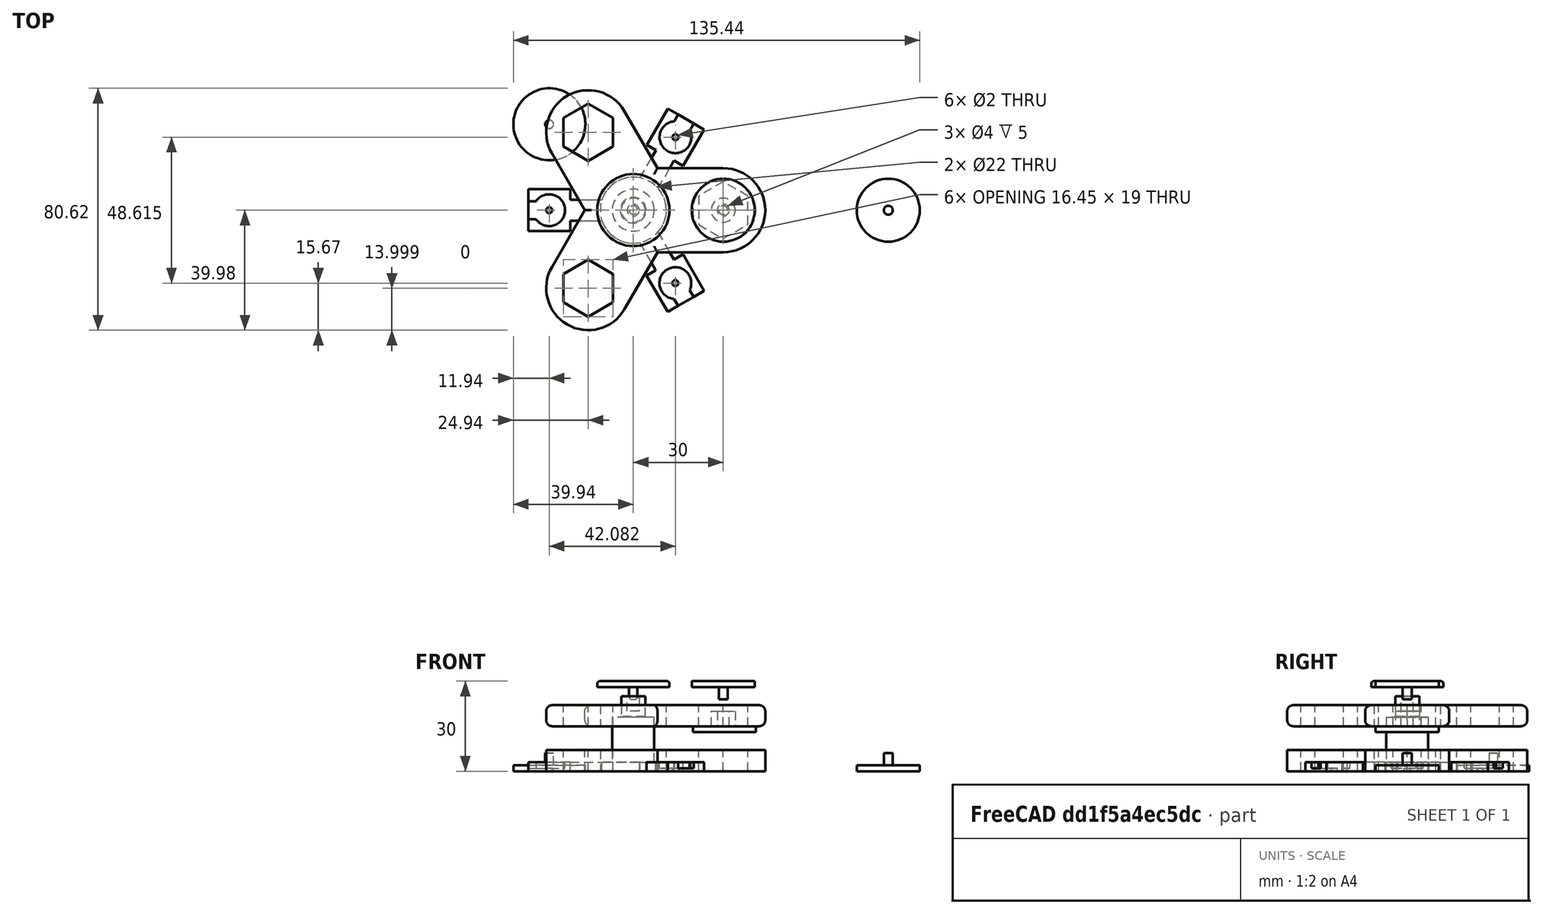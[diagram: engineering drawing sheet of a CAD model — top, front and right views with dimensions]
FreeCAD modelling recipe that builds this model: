
FCSTD DOCUMENT  (FreeCAD 0.17R9747 (Git))
Label: Spinner-ZZ809-M10
License: All rights reserved
LicenseURL: http://en.wikipedia.org/wiki/All_rights_reserved
objects: Sketcher::SketchObject×16, PartDesign::Pad×10, PartDesign::Pocket×6, PartDesign::Body×5, Part::FeaturePython×5, Part::Fillet×4, Mesh::Feature×4, App::DocumentObjectGroup×2, Part::Chamfer×1
note: 63 computed .brp shape members not serialized (recipe doc carries the construction recipe); baked Part::Feature solids carry a one-line shape summary decoded from their .brp

FEATURE [Sketcher::SketchObject] Sketch001  label="Sketch-base"
  MapMode = 5
  Support = -> [XY_Plane001]
  sketch-geometry (28):
    g0: ArcOfCircle CenterX=0.0583268 CenterY=0 CenterZ=0 NormalX=0 NormalY=0 NormalZ=1 Radius=11 StartAngle=3.4654 EndAngle=4.90733
    g1: LineSegment [constr] StartX=0 StartY=0 StartZ=0 EndX=-28 EndY=0 EndZ=0
    g2: LineSegment [constr] StartX=0 StartY=0 StartZ=0 EndX=14 EndY=24.2487 EndZ=0
    g3: LineSegment [constr] StartX=0 StartY=0 StartZ=0 EndX=14 EndY=-24.2487 EndZ=0
    g4: LineSegment StartX=-35 StartY=7 StartZ=0 EndX=-21 EndY=7 EndZ=0
    g5: LineSegment StartX=-21 StartY=7 StartZ=0 EndX=-21 EndY=3.5 EndZ=0
    g6: LineSegment StartX=-21 StartY=-7 StartZ=0 EndX=-35 EndY=-7 EndZ=0
    g7: LineSegment StartX=-35 StartY=-7 StartZ=0 EndX=-35 EndY=7 EndZ=0
    g8: LineSegment StartX=-21 StartY=3.5 StartZ=0 EndX=-10.37 EndY=3.5 EndZ=0
    g9: LineSegment StartX=-21 StartY=-3.5 StartZ=0 EndX=-10.37 EndY=-3.5 EndZ=0
    g10: LineSegment StartX=-21 StartY=-3.5 StartZ=0 EndX=-21 EndY=-7 EndZ=0
    g11: LineSegment StartX=4.51981 StartY=21.7433 StartZ=0 EndX=7.5509 EndY=19.9933 EndZ=0
    g12: LineSegment StartX=2.23326 StartY=10.7828 StartZ=0 EndX=7.5509 EndY=19.9933 EndZ=0
    g13: LineSegment StartX=8.29808 StartY=7.28742 StartZ=0 EndX=13.6131 EndY=16.4933 EndZ=0
    g14: LineSegment StartX=13.6131 StartY=16.4933 StartZ=0 EndX=16.6442 EndY=14.7433 EndZ=0
    g15: ArcOfCircle CenterX=0.0583268 CenterY=0 CenterZ=0 NormalX=0 NormalY=0 NormalZ=1 Radius=11 StartAngle=1.37176 EndAngle=2.81778
    g16: LineSegment StartX=4.51981 StartY=21.7433 StartZ=0 EndX=11.5198 EndY=33.8676 EndZ=0
    g17: LineSegment StartX=11.5198 StartY=33.8676 StartZ=0 EndX=23.6442 EndY=26.8676 EndZ=0
    g18: LineSegment StartX=16.6442 StartY=14.7433 StartZ=0 EndX=23.6442 EndY=26.8676 EndZ=0
    g19: LineSegment [constr] StartX=14 StartY=24.2487 StartZ=0 EndX=17.0311 EndY=22.4987 EndZ=0
    g20: LineSegment StartX=4.47302 StartY=-21.7475 StartZ=0 EndX=7.50411 EndY=-19.9975 EndZ=0
    g21: LineSegment StartX=8.26824 StartY=-7.32102 StartZ=0 EndX=13.5663 EndY=-16.4975 EndZ=0
    g22: LineSegment StartX=2.18911 StartY=-10.7917 StartZ=0 EndX=7.50411 EndY=-19.9975 EndZ=0
    g23: ArcOfCircle CenterX=0.0583268 CenterY=0 CenterZ=0 NormalX=0 NormalY=0 NormalZ=1 Radius=11 StartAngle=5.55496 EndAngle=7.00733
    g24: LineSegment StartX=13.5663 StartY=-16.4975 StartZ=0 EndX=16.5974 EndY=-14.7475 EndZ=0
    g25: LineSegment StartX=16.5974 StartY=-14.7475 StartZ=0 EndX=23.5974 EndY=-26.8719 EndZ=0
    g26: LineSegment StartX=23.5974 StartY=-26.8719 StartZ=0 EndX=11.473 EndY=-33.8719 EndZ=0
    g27: LineSegment StartX=11.473 StartY=-33.8719 StartZ=0 EndX=4.47302 EndY=-21.7475 EndZ=0
  constraints (83):
    c: Coincident(g1,g-1)
    c: Coincident(g2,g-1)
    c: Coincident(g3,g-1)
    c: Equal(g1,g2)
    c: Equal(g2,g3)
    c: Angle(g2,g1) = 2.0944
    c: Angle(g3,g2) = 2.0944
    c: DistanceX(g1,g1) = 28
    c: Coincident(g4,g5)
    c: Coincident(g10,g6)
    c: Coincident(g6,g7)
    c: Coincident(g7,g4)
    c: Horizontal(g4)
    c: Horizontal(g6)
    c: Vertical(g5)
    c: Vertical(g7)
    c: Symmetric(g4,g10,g1)
    c: DistanceX(g4,g4) = 14
    c: Radius(g0) = 11
    c: Horizontal(g8)
    c: Horizontal(g9)
    c: Tangent(g5,g10)
    c: Coincident(g9,g0)
    c: Coincident(g8,g15)
    c: Coincident(g8,g5)
    c: Coincident(g10,g9)
    c: DistanceY(g9,g5) = 7
    c: DistanceY(g7,g7) = 14
    c: DistanceY(g10,g10) = 3.5
    c: Equal(g8,g9)
    c: Symmetric(g0,g15,g1)
    c: DistanceX(g9,g9) = 10.63
    c: Angle(g14,g2) = 1.5708
    c: Angle(g12,g11) = 1.5708
    c: Parallel(g2,g12)
    c: Parallel(g2,g13)
    c: Coincident(g11,g12)
    c: Tangent(g11,g14)
    c: Equal(g0,g15)
    c: Coincident(g0,g15)
    c: Coincident(g12,g15)
    c: Coincident(g13,g23)
    c: Coincident(g13,g14)
    c: Distance(g12,g23) = 7
    c: Equal(g14,g11)
    c: Distance(g11) = 3.5
    c: Coincident(g16,g11)
    c: Coincident(g17,g16)
    c: Coincident(g18,g14)
    c: Coincident(g18,g17)
    c: Distance(g13) = 10.63
    c: Angle(g16,g17) = 1.5708
    c: Distance(g17) = 14
    c: Equal(g18,g17)
    c: Equal(g17,g16)
    c: Coincident(g19,g2)
    c: Angle(g2,g19) = 1.5708
    c: Distance(g19) = 3.5
    c: Distance(g13,g19) = 6.91
    c: Angle(g3,g24) = 1.5708
    c: Parallel(g21,g3)
    c: Parallel(g22,g3)
    c: Equal(g0,g23)
    c: Coincident(g0,g23)
    c: Tangent(g20,g24)
    c: Coincident(g21,g24)
    c: Coincident(g22,g20)
    c: Coincident(g22,g0)
    c: Coincident(g21,g23)
    c: Equal(g20,g24)
    c: Distance(g24) = 3.5
    c: Distance(g0,g21) = 7
    c: Symmetric(g20,g21,g3)
    c: Distance(g22) = 10.63
    c: Coincident(g24,g25)
    c: Coincident(g25,g26)
    c: Coincident(g26,g27)
    c: Coincident(g27,g20)
    c: Angle(g25,g26) = 1.5708
    c: Angle(g26,g27) = 1.5708
    c: Distance(g26) = 14
    c: Equal(g27,g25)
    c: Equal(g25,g26)
FEATURE [PartDesign::Pad] Pad  label="Base-inicial"
  Length = 3
  Length2 = 100
  Profile = -> Sketch001
  Type = 0
FEATURE [Sketcher::SketchObject] Sketch  label="Sketch-rebajes-chinchetas"
  ExternalGeometry = -> [Pad]
  MapMode = 5
  Placement = pos=(0,0,3) rot=(0,0,1;0rad)
  Support = -> [Pad]
  sketch-geometry (20):
    g0: LineSegment [constr] StartX=-35 StartY=7 StartZ=0 EndX=-21 EndY=-7 EndZ=0
    g1: LineSegment [constr] StartX=-35 StartY=-7 StartZ=0 EndX=-28 EndY=-3e-12 EndZ=0
    g2: ArcOfCircle CenterX=-28 CenterY=-3e-12 CenterZ=0 NormalX=0 NormalY=0 NormalZ=1 Radius=5.3 StartAngle=3.74328 EndAngle=8.82309
    g3: LineSegment StartX=-36.3692 StartY=3 StartZ=0 EndX=-32.3692 EndY=3 EndZ=0
    g4: LineSegment StartX=-36.3692 StartY=-3 StartZ=0 EndX=-32.3692 EndY=-3 EndZ=0
    g5: LineSegment StartX=-36.3692 StartY=3 StartZ=0 EndX=-36.3692 EndY=-3 EndZ=0
    g6: LineSegment [constr] StartX=4.47302 StartY=-21.7475 StartZ=0 EndX=23.5974 EndY=-26.8719 EndZ=0
    g7: LineSegment [constr] StartX=14.0352 StartY=-24.3097 StartZ=0 EndX=16.5974 EndY=-14.7475 EndZ=0
    g8: LineSegment [constr] StartX=0 StartY=0 StartZ=0 EndX=19 EndY=-32.909 EndZ=0
    g9: LineSegment [constr] StartX=4.51981 StartY=21.7433 StartZ=0 EndX=14.082 EndY=24.3054 EndZ=0
    g10: LineSegment [constr] StartX=11.5198 StartY=33.8676 StartZ=0 EndX=16.6442 EndY=14.7433 EndZ=0
    g11: LineSegment [constr] StartX=0 StartY=0 StartZ=0 EndX=19.0499 EndY=32.8801 EndZ=0
    g12: ArcOfCircle CenterX=14.0352 CenterY=-24.3097 CenterZ=0 NormalX=0 NormalY=0 NormalZ=1 Radius=5.3 StartAngle=5.83768 EndAngle=10.9175
    g13: ArcOfCircle CenterX=14.082 CenterY=24.3054 CenterZ=0 NormalX=0 NormalY=0 NormalZ=1 Radius=5.3 StartAngle=1.64834 EndAngle=6.72621
    g14: LineSegment StartX=16.4019 StartY=-34.409 StartZ=0 EndX=13.6217 EndY=-29.5935 EndZ=0
    g15: LineSegment StartX=21.5981 StartY=-31.409 StartZ=0 EndX=18.8179 EndY=-26.5935 EndZ=0
    g16: LineSegment StartX=16.4019 StartY=-34.409 StartZ=0 EndX=21.5981 EndY=-31.409 EndZ=0
    g17: LineSegment StartX=13.6714 StartY=29.5895 StartZ=0 EndX=16.4505 EndY=34.3861 EndZ=0
    g18: LineSegment StartX=16.4505 StartY=34.3861 StartZ=0 EndX=21.6421 EndY=31.3783 EndZ=0
    g19: LineSegment StartX=21.6421 StartY=31.3783 StartZ=0 EndX=18.8703 EndY=26.5774 EndZ=0
  constraints (58):
    c: Coincident(g0,g-4)
    c: Coincident(g1,g-4)
    c: PointOnObject(g1,g0)
    c: Coincident(g2,g1)
    c: Radius(g2) = 5.3
    c: Coincident(g0,g-5)
    c: Angle(g-4,g1) = 0.785398
    c: Horizontal(g3)
    c: Horizontal(g4)
    c: Coincident(g2,g4)
    c: Coincident(g2,g3)
    c: DistanceY(g2,g2) = 6
    c: Equal(g3,g4)
    c: Coincident(g5,g3)
    c: Vertical(g5)
    c: Coincident(g5,g4)
    c: DistanceX(g3,g3) = 4
    c: Coincident(g6,g-6)
    c: Coincident(g6,g-8)
    c: Coincident(g7,g-7)
    c: PointOnObject(g7,g6)
    c: Angle(g7,g-7) = 0.785398
    c: Coincident(g8,g-1)
    c: PointOnObject(g7,g8)
    c: Distance(g8) = 38
    c: Coincident(g9,g-9)
    c: Coincident(g10,g-10)
    c: Coincident(g10,g-11)
    c: PointOnObject(g9,g10)
    c: Angle(g9,g-9) = 0.785398
    c: Coincident(g11,g-1)
    c: PointOnObject(g9,g11)
    c: Distance(g11) = 38
    c: Coincident(g12,g7)
    c: Radius(g12) = 5.3
    c: Coincident(g13,g9)
    c: Radius(g13) = 5.3
    c: Parallel(g15,g14)
    c: PointOnObject(g12,g14)
    c: Coincident(g12,g15)
    c: Symmetric(g12,g12,g8)
    c: Distance(g14,g15) = 6
    c: PointOnObject(g8,g16)
    c: Coincident(g14,g16)
    c: Coincident(g15,g16)
    c: Coincident(g12,g14)
    c: Angle(g14,g-8) = 1.5708
    c: Equal(g15,g14)
    c: Coincident(g17,g18)
    c: Coincident(g18,g19)
    c: Coincident(g17,g13)
    c: PointOnObject(g11,g18)
    c: Angle(g19,g-10) = 1.5708
    c: Angle(g17,g18) = 1.5708
    c: Distance(g18) = 6
    c: Coincident(g13,g19)
    c: Symmetric(g13,g13,g11)
    c: Equal(g17,g19)
FEATURE [PartDesign::Pocket] Pocket  label="Rebajes-chinchetas"
  BaseFeature = -> Pad
  Length = 2
  Profile = -> Sketch
  Type = 0
FEATURE [Sketcher::SketchObject] Sketch002  label="Sketch-agujero-chincheta-1"
  ExternalGeometry = -> [Pocket]
  MapMode = 5
  Placement = pos=(0,0,1) rot=(0,0,1;0rad)
  Support = -> [Pocket]
  sketch-geometry (1):
    g0: Circle CenterX=-28 CenterY=-3e-12 CenterZ=0 NormalX=0 NormalY=0 NormalZ=1 Radius=1
  constraints (2):
    c: Coincident(g0,g-3)
    c: Radius(g0) = 1
FEATURE [PartDesign::Pocket] Pocket001  label="Agujero-chincheta-1"
  BaseFeature = -> Pocket
  Length = 5
  Profile = -> Sketch002
  Type = 0
FEATURE [Sketcher::SketchObject] Sketch003  label="Sketch-agujero-chincheta-2"
  ExternalGeometry = -> [Pocket001]
  MapMode = 5
  Placement = pos=(0,0,1) rot=(0,0,1;0rad)
  Support = -> [Pocket001]
  sketch-geometry (1):
    g0: Circle CenterX=14.082 CenterY=24.3054 CenterZ=0 NormalX=0 NormalY=0 NormalZ=1 Radius=1
  constraints (2):
    c: Coincident(g0,g-3)
    c: Radius(g0) = 1
FEATURE [PartDesign::Pocket] Pocket002  label="Agujero-chincheta-2"
  BaseFeature = -> Pocket001
  Length = 5
  Profile = -> Sketch003
  Type = 0
FEATURE [Sketcher::SketchObject] Sketch004  label="Sketch-agujero-chincheta-3"
  ExternalGeometry = -> [Pocket002]
  MapMode = 5
  Placement = pos=(0,0,1) rot=(0,0,1;0rad)
  Support = -> [Pocket002]
  sketch-geometry (1):
    g0: Circle CenterX=14.0352 CenterY=-24.3097 CenterZ=0 NormalX=0 NormalY=0 NormalZ=1 Radius=1
  constraints (2):
    c: Coincident(g0,g-3)
    c: Radius(g0) = 1
FEATURE [PartDesign::Pocket] Pocket003  label="Base-con-chinchetas"
  BaseFeature = -> Pocket002
  Length = 5
  Profile = -> Sketch004
  Type = 0
FEATURE [Sketcher::SketchObject] Sketch005  label="Sketch-tope-inferior"
  MapMode = 5
  Placement = pos=(0,0,3) rot=(0,0,1;0rad)
  Support = -> [Pocket003]
  sketch-geometry (1):
    g0: Circle CenterX=0 CenterY=0 CenterZ=0 NormalX=0 NormalY=0 NormalZ=1 Radius=7
  constraints (2):
    c: Coincident(g0,g-1)
    c: Radius(g0) = 7
FEATURE [PartDesign::Pad] Pad001  label="Tope-inferior"
  BaseFeature = -> Pocket003
  Length = 15
  Length2 = 100
  Profile = -> Sketch005
  Type = 0
FEATURE [Sketcher::SketchObject] Sketch006  label="Sketch-eje"
  MapMode = 5
  Placement = pos=(0,0,18) rot=(0,0,1;0rad)
  Support = -> [Pad001]
  sketch-geometry (1):
    g0: Circle CenterX=0 CenterY=0 CenterZ=0 NormalX=0 NormalY=0 NormalZ=1 Radius=4
  constraints (2):
    c: Coincident(g0,g-1)
    c: Radius(g0) = 4
FEATURE [PartDesign::Pad] Pad002  label="Eje-inicial"
  BaseFeature = -> Pad001
  Length = 7
  Length2 = 100
  Profile = -> Sketch006
  Type = 0
FEATURE [Sketcher::SketchObject] Sketch007  label="Sketch-agujero-tapa"
  MapMode = 5
  Placement = pos=(0,0,25) rot=(0,0,1;0rad)
  Support = -> [Pad002]
  sketch-geometry (1):
    g0: Circle CenterX=0 CenterY=0 CenterZ=0 NormalX=0 NormalY=0 NormalZ=1 Radius=2
  constraints (2):
    c: Coincident(g0,g-1)
    c: Radius(g0) = 2
FEATURE [PartDesign::Pocket] Pocket004  label="Base-final-bruto"
  BaseFeature = -> Pad002
  Length = 5
  Profile = -> Sketch007
  Type = 0
FEATURE [PartDesign::Body] Body001  label="BodyBase"
  Group = -> [Sketch001,Pad,Sketch,Pocket,Sketch002,Pocket001,Sketch003,Pocket002,Sketch004,Pocket003,Sketch005,Pad001,Sketch006,Pad002,Sketch007,Pocket004]
  Origin = -> Body001Origin
  Tip = -> Pocket004
FEATURE [Part::Chamfer] Chamfer
  Base = -> Pocket004
  Edges = 1 edges r=0.3: [Edge121]
FEATURE [Part::Fillet] Fillet  label="Base-final"
  Base = -> Chamfer
  Edges = 1 edges r=0.8: [Edge8]
  Placement = pos=(-60,0,0) rot=(0,0,1;0rad)
FEATURE [Sketcher::SketchObject] Sketch008  label="Sketch-base-tapa"
  MapMode = 5
  Support = -> [XY_Plane]
  sketch-geometry (1):
    g0: Circle CenterX=-27.942 CenterY=28.6445 CenterZ=0 NormalX=0 NormalY=0 NormalZ=1 Radius=12
  constraints (1):
    c: Radius(g0) = 12
FEATURE [PartDesign::Pad] Pad003  label="Base-tapa-inicial"
  Length = 2
  Length2 = 100
  Profile = -> Sketch008
  Type = 0
FEATURE [Sketcher::SketchObject] Sketch009  label="Sketch-eje-tapa"
  ExternalGeometry = -> [Pad003]
  MapMode = 5
  Placement = pos=(0,0,2) rot=(0,0,1;0rad)
  Support = -> [Pad003]
  sketch-geometry (1):
    g0: Circle CenterX=-27.942 CenterY=28.6445 CenterZ=0 NormalX=0 NormalY=0 NormalZ=1 Radius=1.4
  constraints (2):
    c: Coincident(g0,g-3)
    c: Radius(g0) = 1.4
FEATURE [PartDesign::Pad] Pad004  label="Tapa-con-eje"
  BaseFeature = -> Pad003
  Length = 4
  Length2 = 100
  Profile = -> Sketch009
  Type = 0
FEATURE [PartDesign::Body] Body  label="BodyTapa-simple"
  Group = -> [Sketch008,Pad003,Sketch009,Pad004]
  Origin = -> BodyOrigin
  Tip = -> Pad004
FEATURE [Part::Fillet] Fillet001
  Base = -> Pad004
  Edges = 1 edges r=0.8: [Edge2]
FEATURE [Part::Fillet] Fillet002  label="Tapa"
  Base = -> Fillet001
  Edges = 1 edges r=0.7: [Edge8]
  Placement = pos=(-47,0,0) rot=(0,0,1;0rad)
FEATURE [Part::FeaturePython] Clone  label="Base-final001"  # Draft clone (typed FeaturePython)
  AttacherType = Attacher::AttachEngine3D
  Objects = -> [Fillet]
  Scale = (1,1,1)
FEATURE [Part::FeaturePython] Clone001  label="Tapa001"  # Draft clone (typed FeaturePython)
  AttacherType = Attacher::AttachEngine3D
  Objects = -> [Fillet002]
  Placement = pos=(-27.9,-28.6,30) rot=(0,1,0;3.14159rad)
  Scale = (1,1,1)
FEATURE [Sketcher::SketchObject] Sketch011  label="Sketch-spinner-inicial"
  MapMode = 5
  Support = -> [XY_Plane002]
  sketch-geometry (37):
    g0: LineSegment [constr] StartX=0 StartY=0 StartZ=0 EndX=30 EndY=0 EndZ=0
    g1: LineSegment [constr] StartX=0 StartY=0 StartZ=0 EndX=-15 EndY=25.9808 EndZ=0
    g2: LineSegment [constr] StartX=0 StartY=0 StartZ=0 EndX=-15 EndY=-25.9808 EndZ=0
    g3: LineSegment [constr] StartX=-27.1244 StartY=-18.9808 StartZ=0 EndX=-2.87564 EndY=-32.9808 EndZ=0
    g4: LineSegment [constr] StartX=30 StartY=14 StartZ=0 EndX=30 EndY=-14 EndZ=0
    g5: LineSegment [constr] StartX=-27.1244 StartY=18.9808 StartZ=0 EndX=-2.87564 EndY=32.9808 EndZ=0
    g6: Circle CenterX=0 CenterY=0 CenterZ=0 NormalX=0 NormalY=0 NormalZ=1 Radius=11
    g7: LineSegment StartX=-2.87564 StartY=32.9808 StartZ=0 EndX=8.0829 EndY=14 EndZ=0
    g8: LineSegment StartX=8.0829 StartY=14 StartZ=0 EndX=30 EndY=14 EndZ=0
    g9: LineSegment StartX=30 StartY=-14 StartZ=0 EndX=8.0829 EndY=-14 EndZ=0
    g10: LineSegment StartX=8.0829 StartY=-14 StartZ=0 EndX=-2.87564 EndY=-32.9808 EndZ=0
    g11: LineSegment StartX=-27.1244 StartY=18.9808 StartZ=0 EndX=-16.1658 EndY=0 EndZ=0
    g12: LineSegment StartX=-16.1658 StartY=0 StartZ=0 EndX=-27.1244 EndY=-18.9808 EndZ=0
    g13: ArcOfCircle CenterX=-15 CenterY=25.9808 CenterZ=0 NormalX=0 NormalY=0 NormalZ=1 Radius=14 StartAngle=0.523599 EndAngle=3.66519
    g14: ArcOfCircle CenterX=30 CenterY=0 CenterZ=0 NormalX=0 NormalY=0 NormalZ=1 Radius=14 StartAngle=4.71239 EndAngle=7.85398
    g15: ArcOfCircle CenterX=-15 CenterY=-25.9808 CenterZ=0 NormalX=0 NormalY=0 NormalZ=1 Radius=14 StartAngle=2.61799 EndAngle=5.75959
    g16: LineSegment StartX=-6.77276 StartY=21.2308 StartZ=0 EndX=-6.77276 EndY=30.7308 EndZ=0
    g17: LineSegment StartX=-6.77276 StartY=30.7308 StartZ=0 EndX=-15 EndY=35.4808 EndZ=0
    g18: LineSegment StartX=-15 StartY=35.4808 StartZ=0 EndX=-23.2272 EndY=30.7308 EndZ=0
    g19: LineSegment StartX=-23.2272 StartY=30.7308 StartZ=0 EndX=-23.2272 EndY=21.2308 EndZ=0
    g20: LineSegment StartX=-23.2272 StartY=21.2308 StartZ=0 EndX=-15 EndY=16.4808 EndZ=0
    g21: LineSegment StartX=-15 StartY=16.4808 StartZ=0 EndX=-6.77276 EndY=21.2308 EndZ=0
    g22: Circle [constr] CenterX=-15 CenterY=25.9808 CenterZ=0 NormalX=0 NormalY=0 NormalZ=1 Radius=9.5
    g23: LineSegment StartX=30 StartY=-9.5 StartZ=0 EndX=38.2272 EndY=-4.75 EndZ=0
    g24: LineSegment StartX=38.2272 StartY=-4.75 StartZ=0 EndX=38.2272 EndY=4.75 EndZ=0
    g25: LineSegment StartX=38.2272 StartY=4.75 StartZ=0 EndX=30 EndY=9.5 EndZ=0
    g26: LineSegment StartX=30 StartY=9.5 StartZ=0 EndX=21.7728 EndY=4.75 EndZ=0
    g27: LineSegment StartX=21.7728 StartY=4.75 StartZ=0 EndX=21.7728 EndY=-4.75 EndZ=0
    g28: LineSegment StartX=21.7728 StartY=-4.75 StartZ=0 EndX=30 EndY=-9.5 EndZ=0
    g29: Circle [constr] CenterX=30 CenterY=0 CenterZ=0 NormalX=0 NormalY=0 NormalZ=1 Radius=9.5
    g30: LineSegment StartX=-6.77276 StartY=-30.7308 StartZ=0 EndX=-6.77276 EndY=-21.2308 EndZ=0
    g31: LineSegment StartX=-6.77276 StartY=-21.2308 StartZ=0 EndX=-15 EndY=-16.4808 EndZ=0
    g32: LineSegment StartX=-15 StartY=-16.4808 StartZ=0 EndX=-23.2272 EndY=-21.2308 EndZ=0
    g33: LineSegment StartX=-23.2272 StartY=-21.2308 StartZ=0 EndX=-23.2272 EndY=-30.7308 EndZ=0
    g34: LineSegment StartX=-23.2272 StartY=-30.7308 StartZ=0 EndX=-15 EndY=-35.4808 EndZ=0
    g35: LineSegment StartX=-15 StartY=-35.4808 StartZ=0 EndX=-6.77276 EndY=-30.7308 EndZ=0
    g36: Circle [constr] CenterX=-15 CenterY=-25.9808 CenterZ=0 NormalX=0 NormalY=0 NormalZ=1 Radius=9.5
  constraints (95):
    c: Coincident(g0,g-1)
    c: PointOnObject(g0,g-1)
    c: Coincident(g1,g-1)
    c: Coincident(g2,g-1)
    c: Equal(g0,g1)
    c: Equal(g1,g2)
    c: Angle(g0,g1) = 2.0944
    c: Angle(g1,g2) = 2.0944
    c: DistanceX(g0,g0) = 30
    c: Vertical(g4)
    c: PointOnObject(g2,g3)
    c: Angle(g3,g2) = 1.5708
    c: Distance(g3) = 28
    c: PointOnObject(g0,g4)
    c: DistanceY(g4,g4) = 28
    c: PointOnObject(g1,g5)
    c: Distance(g5) = 28
    c: Coincident(g6,g-1)
    c: Radius(g6) = 11
    c: Distance(g2,g3) = 14
    c: Distance(g5,g1) = 14
    c: Coincident(g7,g5)
    c: Coincident(g8,g4)
    c: Horizontal(g8)
    c: Equal(g7,g8)
    c: Coincident(g7,g8)
    c: Coincident(g4,g9)
    c: Horizontal(g9)
    c: Coincident(g9,g10)
    c: Coincident(g10,g3)
    c: Equal(g10,g9)
    c: Equal(g9,g8)
    c: Coincident(g5,g11)
    c: PointOnObject(g11,g-1)
    c: Coincident(g11,g12)
    c: Coincident(g12,g3)
    c: Equal(g12,g11)
    c: Equal(g11,g7)
    c: Coincident(g13,g1)
    c: Coincident(g13,g5)
    c: Coincident(g13,g5)
    c: Coincident(g14,g0)
    c: Coincident(g14,g4)
    c: Coincident(g14,g4)
    c: Coincident(g15,g2)
    c: Coincident(g15,g3)
    c: Coincident(g15,g3)
    c: Coincident(g16,g17)
    c: Coincident(g17,g18)
    c: Coincident(g18,g19)
    c: Coincident(g19,g20)
    c: Coincident(g20,g21)
    c: Coincident(g21,g16)
    c: Equal(g16, g17-g21) x5
    c: PointOnObject(g16,g22)
    c: PointOnObject(g17,g22)
    c: PointOnObject(g18,g22)
    c: PointOnObject(g19,g22)
    c: PointOnObject(g20,g22)
    c: PointOnObject(g21,g22)
    c: Coincident(g22,g1)
    c: Radius(g22) = 9.5
    c: PointOnObject(g19,g5)
    c: Coincident(g23,g24)
    c: Coincident(g24,g25)
    c: Coincident(g25,g26)
    c: Coincident(g26,g27)
    c: Coincident(g27,g28)
    c: Coincident(g28,g23)
    c: Equal(g23, g24-g28) x5
    c: PointOnObject(g23,g29)
    c: PointOnObject(g24,g29)
    c: PointOnObject(g25,g29)
    c: PointOnObject(g26,g29)
    c: PointOnObject(g27,g29)
    c: PointOnObject(g28,g29)
    c: Coincident(g29,g0)
    c: Equal(g29,g22)
    c: PointOnObject(g23,g4)
    c: Coincident(g30,g31)
    c: Coincident(g31,g32)
    c: Coincident(g32,g33)
    c: Coincident(g33,g34)
    c: Coincident(g34,g35)
    c: Coincident(g35,g30)
    c: Equal(g30, g31-g35) x5
    c: PointOnObject(g30,g36)
    c: PointOnObject(g31,g36)
    c: PointOnObject(g32,g36)
    c: PointOnObject(g33,g36)
    c: PointOnObject(g34,g36)
    c: PointOnObject(g35,g36)
    c: Coincident(g36,g2)
    c: Equal(g36,g29)
    c: PointOnObject(g30,g3)
FEATURE [PartDesign::Pad] Pad005  label="Spinner-inicial"
  Length = 7
  Length2 = 100
  Profile = -> Sketch011
  Type = 0
FEATURE [PartDesign::Body] Body002  label="BodySpinner"
  Group = -> [Sketch011,Pad005]
  Origin = -> Body002Origin
  Tip = -> Pad005
FEATURE [Part::Fillet] Fillet003  label="Spinner"
  Base = -> Pad005
  Edges = 18 edges r=2: [Edge3,Edge4,Edge6,Edge7,Edge9,Edge10,Edge12,Edge13,Edge15,Edge16,Edge18,Edge19,Edge21,Edge22,Edge24,Edge25,Edge26,Edge27]
FEATURE [Part::FeaturePython] Clone002  label="Spinner001"  # Draft clone (typed FeaturePython)
  AttacherType = Attacher::AttachEngine3D
  Objects = -> [Fillet003]
  Placement = pos=(0,0,15) rot=(0,0,1;0rad)
  Scale = (1,1,1)
FEATURE [Sketcher::SketchObject] Sketch012  label="Sketch-inicio"
  MapMode = 5
  Support = -> [XY_Plane003]
  sketch-geometry (1):
    g0: Circle CenterX=-0.354757 CenterY=0 CenterZ=0 NormalX=0 NormalY=0 NormalZ=1 Radius=10.5
  constraints (2):
    c: PointOnObject(g0,g-1)
    c: Radius(g0) = 10.5
FEATURE [PartDesign::Pad] Pad006  label="Tapa-tuerca-inicio"
  Length = 2
  Length2 = 100
  Profile = -> Sketch012
  Type = 0
FEATURE [Sketcher::SketchObject] Sketch013
  MapMode = 5
  Placement = pos=(0,0,0) rot=(1,0,0;3.14159rad)
  Support = -> [Pad006]
  sketch-geometry (1):
    g0: Circle CenterX=0 CenterY=0 CenterZ=0 NormalX=0 NormalY=0 NormalZ=1 Radius=4
  constraints (2):
    c: Coincident(g0,g-1)
    c: Radius(g0) = 4
FEATURE [PartDesign::Pad] Pad007  label="Tapa-tuerca-inicial"
  BaseFeature = -> Pad006
  Length = 5
  Length2 = 100
  Profile = -> Sketch013
  Type = 0
FEATURE [Sketcher::SketchObject] Sketch014
  MapMode = 5
  Placement = pos=(0,0,-5) rot=(1,0,0;3.14159rad)
  Support = -> [Pad007]
  sketch-geometry (1):
    g0: Circle CenterX=0 CenterY=0 CenterZ=0 NormalX=0 NormalY=0 NormalZ=1 Radius=2
  constraints (1):
    c: Radius(g0) = 2
FEATURE [PartDesign::Pocket] Pocket005  label="Tapa-tuerca-hembra"
  BaseFeature = -> Pad007
  Length = 5
  Profile = -> Sketch014
  Type = 0
FEATURE [PartDesign::Body] Body003  label="BodyTapa-tuerca-H"
  Group = -> [Sketch012,Pad006,Sketch013,Pad007,Sketch014,Pocket005]
  Origin = -> Body003Origin
  Placement = pos=(60,0,3) rot=(0,1,0;3.14159rad)
FEATURE [Part::FeaturePython] Clone003  label="Tapa-tuerca-hembra001"  # Draft clone (typed FeaturePython)
  AttacherType = Attacher::AttachEngine3D
  Objects = -> [Pocket005]
  Placement = pos=(30,0,15) rot=(0,1,0;3.14159rad)
  Scale = (1,1,1)
FEATURE [Sketcher::SketchObject] Sketch015
  MapMode = 5
  Support = -> [XY_Plane004]
  sketch-geometry (1):
    g0: Circle CenterX=80 CenterY=0 CenterZ=0 NormalX=0 NormalY=0 NormalZ=1 Radius=10.5
  constraints (3):
    c: PointOnObject(g0,g-1)
    c: Radius(g0) = 10.5
    c: DistanceX(g-1,g0) = 80
FEATURE [PartDesign::Pad] Pad008  label="Tapa-tuerca-inicial-m"
  Length = 2
  Length2 = 100
  Profile = -> Sketch015
  Type = 0
FEATURE [Sketcher::SketchObject] Sketch016
  ExternalGeometry = -> [Pad008]
  MapMode = 5
  Placement = pos=(0,0,2) rot=(0,0,1;0rad)
  Support = -> [Pad008]
  sketch-geometry (1):
    g0: Circle CenterX=80 CenterY=0 CenterZ=0 NormalX=0 NormalY=0 NormalZ=1 Radius=1.5
  constraints (2):
    c: Coincident(g0,g-3)
    c: Radius(g0) = 1.5
FEATURE [PartDesign::Pad] Pad009  label="Tapa-tuerca-Macho"
  BaseFeature = -> Pad008
  Length = 4
  Length2 = 100
  Profile = -> Sketch016
  Type = 0
FEATURE [PartDesign::Body] Body004  label="BodyTapa-tuerca-M"
  Group = -> [Sketch015,Pad008,Sketch016,Pad009]
  Origin = -> Body004Origin
  Placement = pos=(5,0,0) rot=(0,0,1;0rad)
  Tip = -> Pad009
FEATURE [App::DocumentObjectGroup] Grupo  label="Design"
  Group = -> [Body001,Fillet,Body,Fillet002,Body002,Fillet003,Body003,Body004]
FEATURE [Part::FeaturePython] Clone004  label="Tapa-tuerca-Macho001"  # Draft clone (typed FeaturePython)
  AttacherType = Attacher::AttachEngine3D
  Objects = -> [Pad009]
  Placement = pos=(110,0,30) rot=(0,1,0;3.14159rad)
  Scale = (1,1,1)
FEATURE [Mesh::Feature] _08zz_bearing  label="608zz_bearing"
  Placement = pos=(0,0,15) rot=(0,0,1;0rad)
FEATURE [Mesh::Feature] DIN_934_Nut_M10  label="DIN-934_Nut_M10"
  Placement = pos=(-15,26,15) rot=(0,0,1;0.785398rad)
FEATURE [Mesh::Feature] DIN_934_Nut_M011  label="DIN-934_Nut_M010-1"
  Placement = pos=(-15,-26,15) rot=(0,0,1;0.785398rad)
FEATURE [Mesh::Feature] DIN_934_Nut_M10001  label="DIN-934_Nut_M010-2"
  Placement = pos=(30,0,15) rot=(0,0,1;0rad)
FEATURE [App::DocumentObjectGroup] Grupo001  label="Ensamble-impresion"
  Group = -> [Clone,Clone001,Clone002,Clone003,Clone004,DIN_934_Nut_M10,DIN_934_Nut_M011,_08zz_bearing,DIN_934_Nut_M10001]
